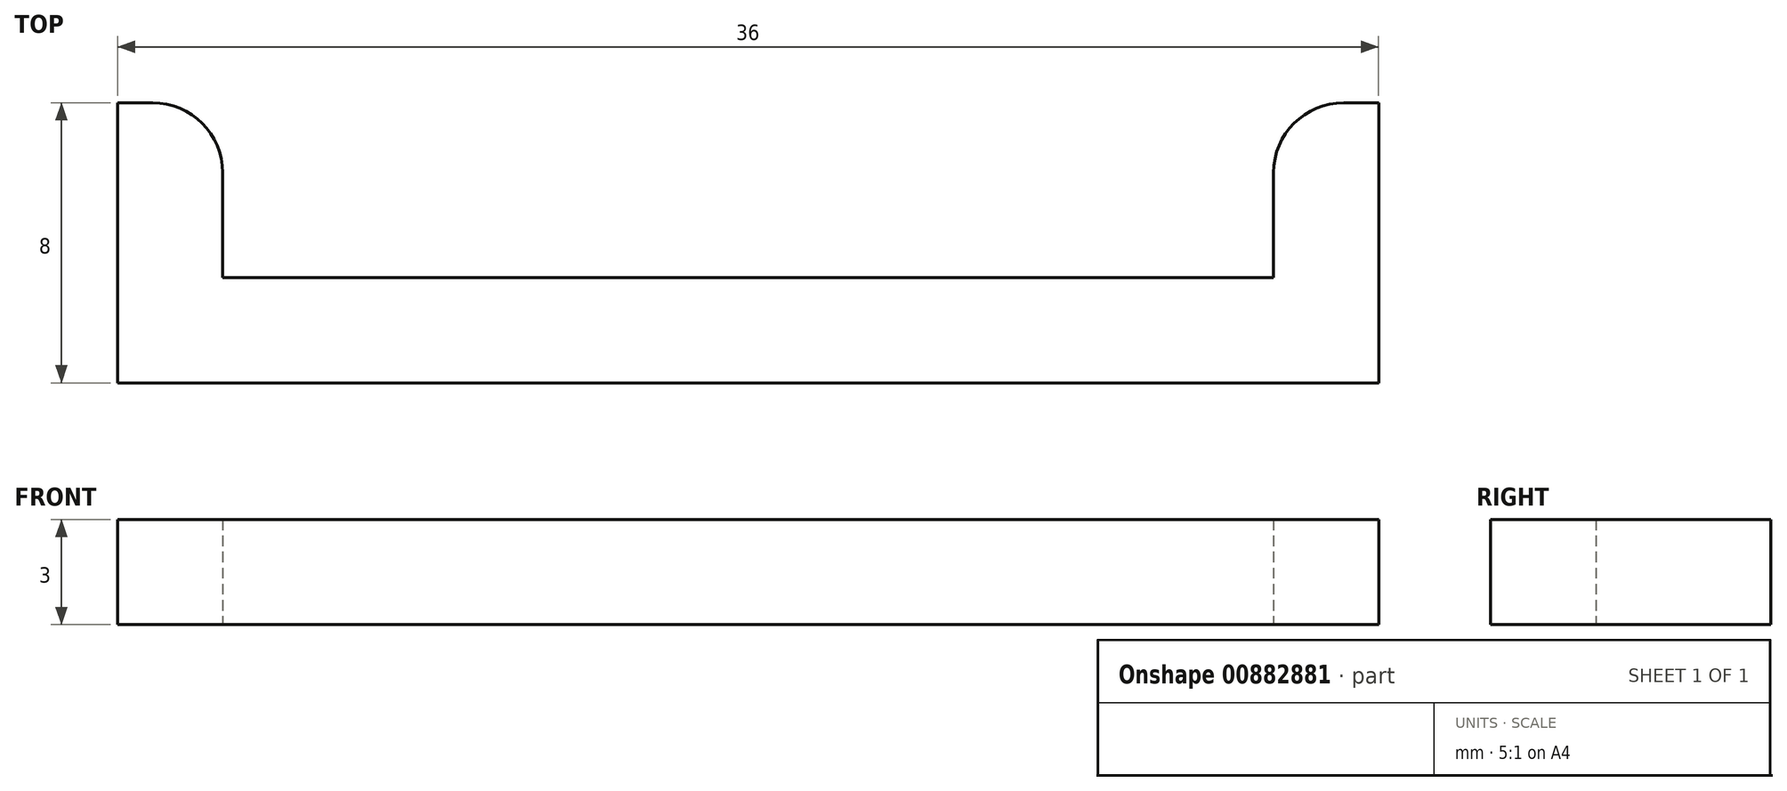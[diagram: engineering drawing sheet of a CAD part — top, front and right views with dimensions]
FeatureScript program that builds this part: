
annotation { "Feature Type Name" : "Feature", "Feature Type Description" : "" }
export const myFeature = defineFeature(function(context is Context, id is Id, definition is map)
    precondition{}
    {
        {
            var Q0;
            Q0=qCreatedBy(makeId("Top.planeOp"),FACE);
            var sketch = newSketch(context, id + "F0", { "sketchPlane" : qUnion([Q0])});
            skLineSegment(sketch, "E0.bottom", {"start": v(10.06, -0.6) * mm, "end": v(-19.94, -0.6) * mm});
            skLineSegment(sketch, "E0.top", {"start": v(10.06, 2.4) * mm, "end": v(-19.94, 2.4) * mm});
            skLineSegment(sketch, "E0.left", {"start": v(10.06, -0.6) * mm, "end": v(10.06, 2.4) * mm});
            skLineSegment(sketch, "E0.right", {"start": v(-19.94, -0.6) * mm, "end": v(-19.94, 2.4) * mm});
            skPoint(sketch, "E0.middle", {"position": v(-4.94, 0.9) * mm});
            skLineSegment(sketch, "E1.bottom", {"start": v(-19.94, -0.6) * mm, "end": v(-22.94, -0.6) * mm});
            skLineSegment(sketch, "E1.top", {"start": v(-21.94, 7.4) * mm, "end": v(-22.94, 7.4) * mm});
            skLineSegment(sketch, "E1.left", {"start": v(-19.94, -0.6) * mm, "end": v(-19.94, 5.4) * mm});
            skLineSegment(sketch, "E1.right", {"start": v(-22.94, -0.6) * mm, "end": v(-22.94, 7.4) * mm});
            skLineSegment(sketch, "E2.bottom", {"start": v(10.06, -0.6) * mm, "end": v(13.06, -0.6) * mm});
            skLineSegment(sketch, "E2.top", {"start": v(12.06, 7.4) * mm, "end": v(13.06, 7.4) * mm});
            skLineSegment(sketch, "E2.left", {"start": v(10.06, -0.6) * mm, "end": v(10.06, 5.4) * mm});
            skLineSegment(sketch, "E2.right", {"start": v(13.06, -0.6) * mm, "end": v(13.06, 7.4) * mm});
            skPoint(sketch, "E3.visualSharp", {"position": v(-19.94, 7.4) * mm});
            skArc(sketch, "E3.filletArc", {"start": v(-19.94, 5.4) * mm, "mid": v(-20.52, 6.82) * mm, "end": v(-21.94, 7.4) * mm});
            skPoint(sketch, "E4.visualSharp", {"position": v(10.06, 7.4) * mm});
            skArc(sketch, "E4.filletArc", {"start": v(12.06, 7.4) * mm, "mid": v(10.65, 6.82) * mm, "end": v(10.06, 5.4) * mm});
            skSolve(sketch);
        }
        {
            var Q0;
            Q0 = qSketchRegion(id + "F0", true);
            extrude(context, id + "F1", {"entities" : qUnion([Q0]), "depth" : 3 * mm, "offsetDistance" : 25 * mm});
        }
    });
